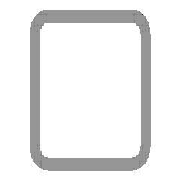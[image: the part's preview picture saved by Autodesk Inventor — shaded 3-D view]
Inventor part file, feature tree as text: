
AUTODESK INVENTOR PART (.ipt)
format: ipt  version: 2022.1 (Build 261234000, 234)  size: 418,304 bytes
history: native  units: mm (DEFAULTED — no unit token found)
features: other x5, plane x5, sketch x4, boolean_combine x2, surface_op x2, split x1, extrude x1
ambient origin geometry x8: Origin, YZ Plane, XZ Plane, XY Plane, X Axis, Y Axis, Z Axis, Center Point
bodies: Solid1 (feature_tree), Body (feature_tree), Solid2 (feature_tree), Solid7 (feature_tree)
feature tree (20):
  parser-record x1  (decoder bookkeeping rows leaked as tree rows — omitted from the tree; the rows remain in map.json)
  other  "Driven Length"
  other  "Start Plane"
  other  "End Plane"
  plane  "Work Plane4"
  split  "Split1"
  plane  "Work Plane5"
  plane  "Work Plane6"
  plane  "Work Plane7"
  extrude  "Extrusion2"  TaperAngle=0.0deg  [1 undecoded]
  boolean_combine  "Combine1"
  surface_op  "Sculpt1"
  boolean_combine  "Combine2"
  sketch  "Sketch"  dims[d11=40.0mm d12=2.0mm d13=-0.0mm d14=211.095123mm d15=20.0mm d16=20.0mm d17=90.0deg d18=211.095123mm d19=0.12mm d20=0.0mm]
  sketch  "Sketch3"  dims[d3=211.095123mm d4=0.0mm]
  plane  "Work Plane3"
  sketch  "Sketch4"  dims[d7=4.0mm]
  sketch  "Sketch5"  dims[d9=40.0mm]
  surface_op  "Surface1"
  other  "Srf13"
note: 1 required parameter value undecoded (feature->parameter linkage not recoverable at this tier; creation-order binding heuristic only, values carry confidence <= 0.55)
